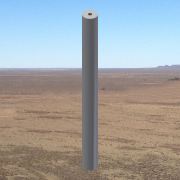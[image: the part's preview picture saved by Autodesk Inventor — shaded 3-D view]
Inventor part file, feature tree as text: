
AUTODESK INVENTOR PART (.ipt)
format: ipt  version: 2014 SP1 (Build 180222100, 222)  size: 146,432 bytes
history: native  units: in
note: dims shown in document units (in); Inventor stores cm internally (conversion verified against a paired STEP export)
features: sketch x3, hole x2, extrude x1
ambient origin geometry x8: Origin, YZ Plane, XZ Plane, XY Plane, X Axis, Y Axis, Z Axis, Center Point
bodies: Solid1 (feature_tree)
feature tree (6):
  extrude  "Extrusion1"  Depth=5.75in TaperAngle=0.0deg
  hole  "Hole1"  [1 undecoded]
  hole  "Hole2"  [1 undecoded]
  sketch  "Sketch1"  dims[d0=0.5in d1=5.75in d2=0.0in]
  sketch  "Sketch2"  dims[d3=0.13in d4=0.5in d5=0.375in d6=0.25in d7=0.5635in d8=0.6in d9=0.8108in]
  sketch  "Sketch3"  dims[d10=0.13in d11=0.5in d12=0.375in d13=0.25in d14=0.5635in d15=0.6in d16=0.8108in]
note: 2 required parameter values undecoded (feature->parameter linkage not recoverable at this tier; creation-order binding heuristic only, values carry confidence <= 0.55)
